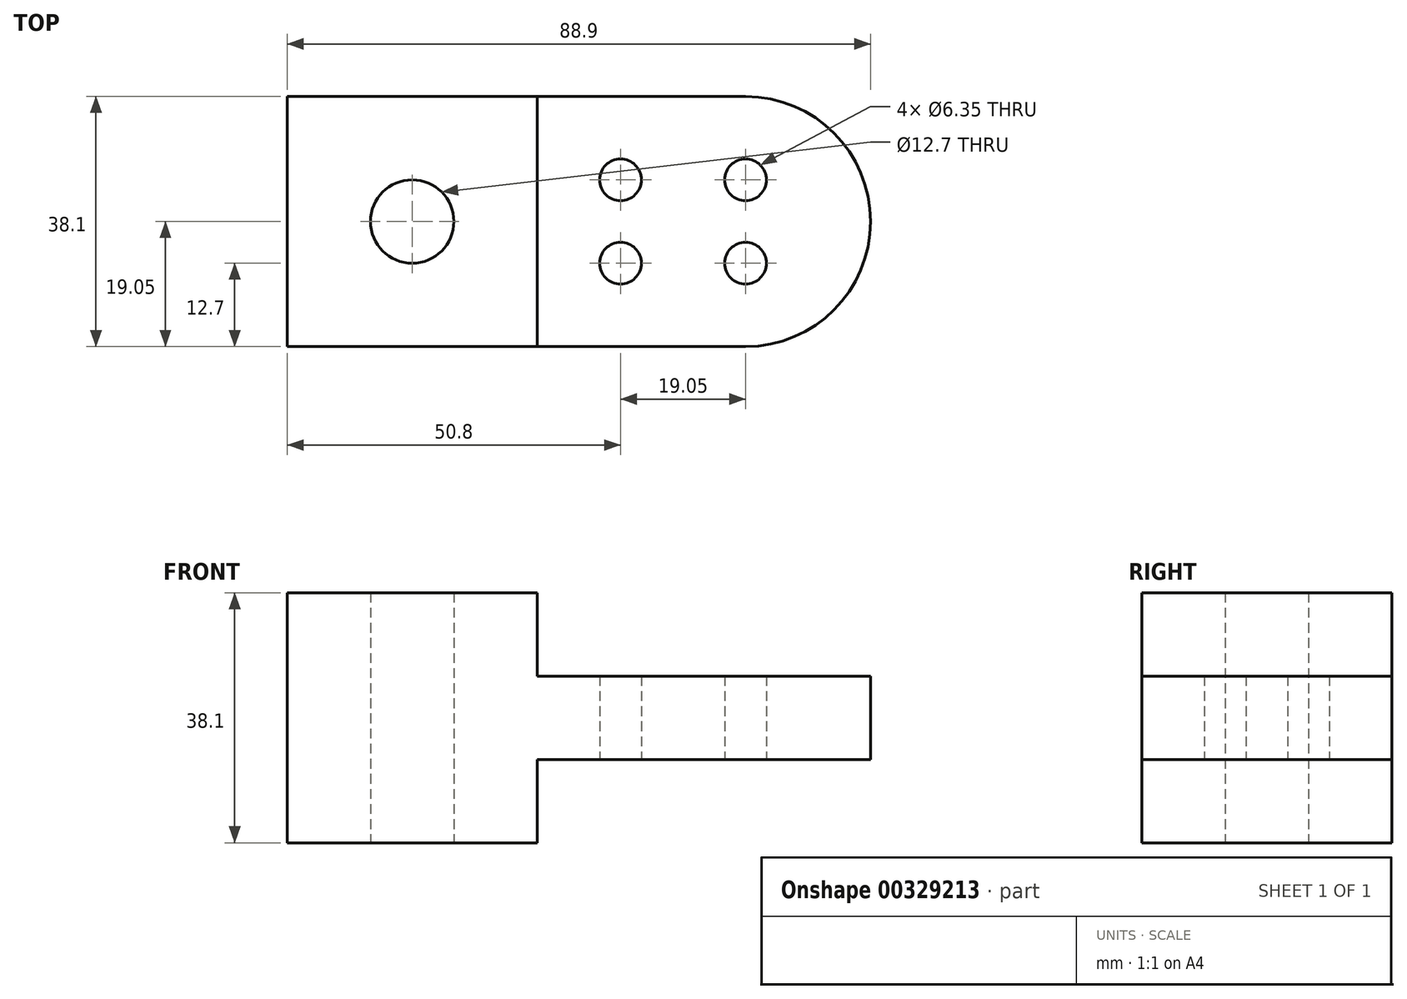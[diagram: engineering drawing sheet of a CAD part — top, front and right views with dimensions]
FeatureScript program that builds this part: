
annotation { "Feature Type Name" : "Feature", "Feature Type Description" : "" }
export const myFeature = defineFeature(function(context is Context, id is Id, definition is map)
    precondition{}
    {
        {
            var Q0;
            Q0=qCreatedBy(makeId("Top.planeOp"),FACE);
            var sketch = newSketch(context, id + "F0", { "sketchPlane" : qUnion([Q0])});
            skLineSegment(sketch, "E0", {"start": v(0, 0) * mm, "end": v(0, 38.1) * mm});
            skLineSegment(sketch, "E1", {"start": v(0, 38.1) * mm, "end": v(69.85, 38.1) * mm});
            skLineSegment(sketch, "E2", {"start": v(0, 0) * mm, "end": v(69.85, 0) * mm});
            skLineSegment(sketch, "E3", {"start": v(38.1, 0) * mm, "end": v(38.1, 38.1) * mm});
            skArc(sketch, "E4", {"start": v(69.85, 0) * mm, "mid": v(88.9, 19.05) * mm, "end": v(69.85, 38.1) * mm});
            skPoint(sketch, "E5", {"position": v(69.85, 25.4) * mm});
            skPoint(sketch, "E6", {"position": v(69.85, 12.7) * mm});
            skPoint(sketch, "E7", {"position": v(50.8, 12.7) * mm});
            skPoint(sketch, "E8", {"position": v(50.8, 25.4) * mm});
            skPoint(sketch, "E9", {"position": v(19.05, 19.05) * mm});
            skCircle(sketch, "E10", {"center": v(19.05, 19.05) * mm, "radius": 6.35 * mm});
            skCircle(sketch, "E11", {"center": v(50.8, 25.4) * mm, "radius": 3.18 * mm});
            skCircle(sketch, "E12", {"center": v(50.8, 12.7) * mm, "radius": 3.18 * mm});
            skCircle(sketch, "E13", {"center": v(69.85, 12.7) * mm, "radius": 3.18 * mm});
            skCircle(sketch, "E14", {"center": v(69.85, 25.4) * mm, "radius": 3.18 * mm});
            skSolve(sketch);
        }
        {
            var Q0;
            {var subQ0=sQuery(id+"F0.wireOp",EDGE,"E0");Q0=makeQuery(id+"F0.imprint","IMPRINT",FACE,{"disambiguationData":[TD([[makeQuery(id+"F0.imprint","IMPRINT",EDGE,{"derivedFrom":subQ0}),-1.0]])]});}
            extrude(context, id + "F1", {"entities" : qUnion([Q0]), "endBound" : BoundingType.SYMMETRIC, "depth" : 38.1 * mm});
        }
        {
            var Q0;
            {var subQ2=sQuery(id+"F0.wireOp",EDGE,"E3");Q0=makeQuery(id+"F0.imprint","IMPRINT",FACE,{"disambiguationData":[TD([[makeQuery(id+"F0.imprint","IMPRINT",EDGE,{"derivedFrom":subQ2}),-1.0]])]});}
            extrude(context, id + "F2", {"entities" : qUnion([Q0]), "operationType" : NewBodyOperationType.ADD, "endBound" : BoundingType.SYMMETRIC, "depth" : 12.7 * mm});
        }
    });
